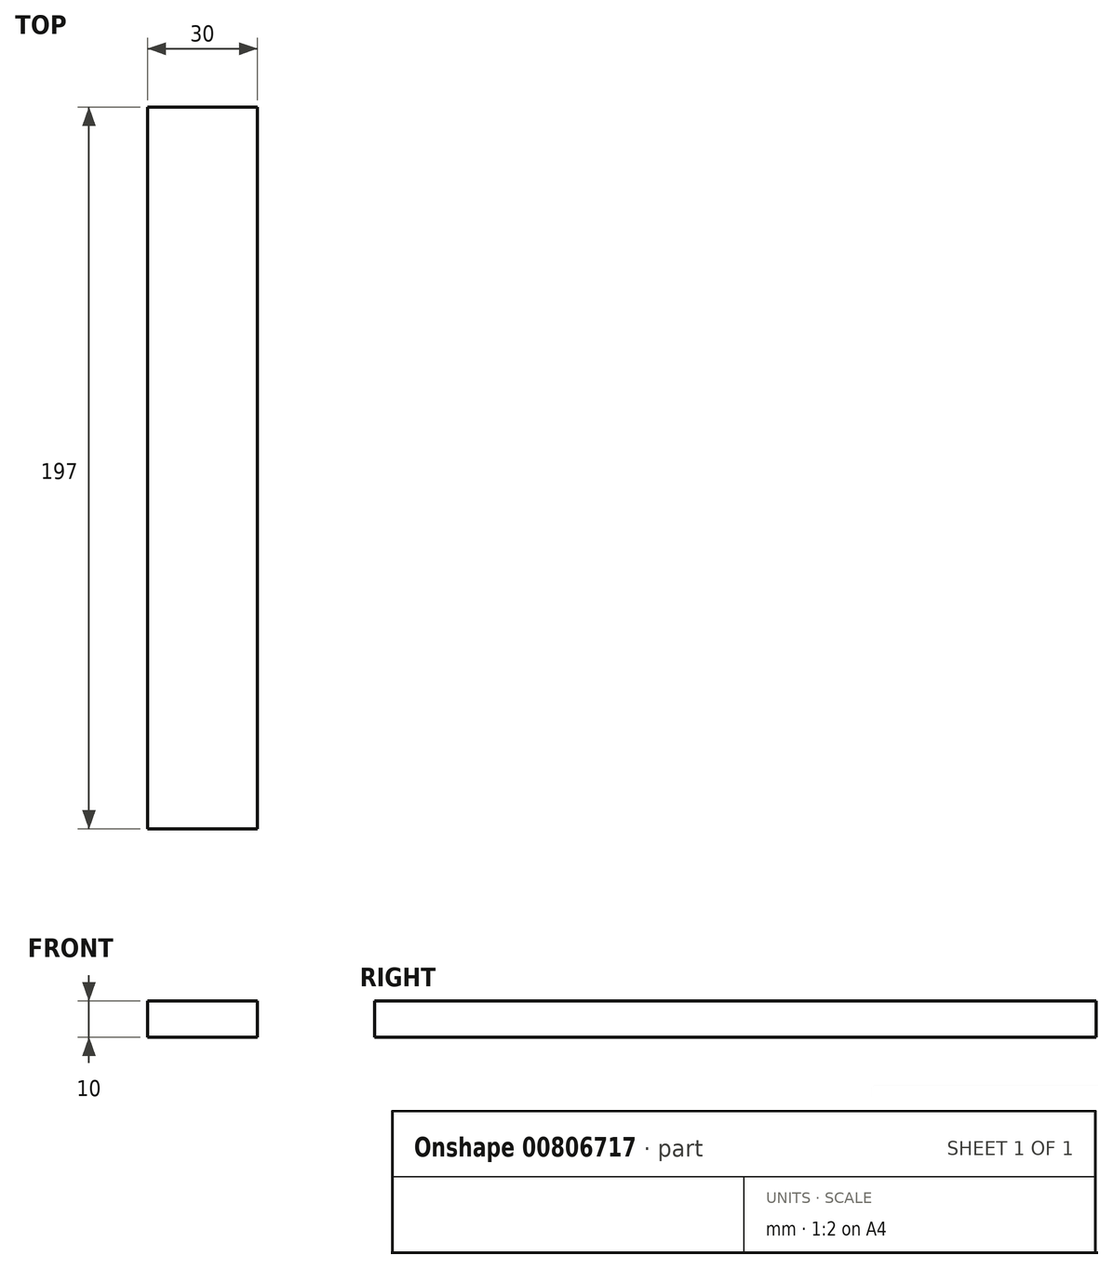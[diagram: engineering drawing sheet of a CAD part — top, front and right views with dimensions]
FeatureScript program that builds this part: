
annotation { "Feature Type Name" : "Feature", "Feature Type Description" : "" }
export const myFeature = defineFeature(function(context is Context, id is Id, definition is map)
    precondition{}
    {
        {
            var Q0;
            Q0=qCreatedBy(makeId("Front.planeOp"),FACE);
            var sketch = newSketch(context, id + "F0", { "sketchPlane" : qUnion([Q0])});
            skLineSegment(sketch, "E0.bottom", {"start": v(0, 0) * mm, "end": v(-30, 0) * mm});
            skLineSegment(sketch, "E0.top", {"start": v(0, 10) * mm, "end": v(-30, 10) * mm});
            skLineSegment(sketch, "E0.left", {"start": v(0, 0) * mm, "end": v(0, 10) * mm});
            skLineSegment(sketch, "E0.right", {"start": v(-30, 0) * mm, "end": v(-30, 10) * mm});
            skSolve(sketch);
        }
        {
            var Q0;
            Q0=makeQuery(id+"F0.imprint","IMPRINT",FACE,{"disambiguationData":[TD([[makeQuery(id+"F0.imprint","IMPRINT",EDGE,{"derivedFrom":sQuery(id+"F0.wireOp",EDGE,"E0.bottom")}),-1.0]])]});
            extrude(context, id + "F1", {"entities" : qUnion([Q0]), "depth" : 197 * mm, "offsetDistance" : 25 * mm});
        }
    });
